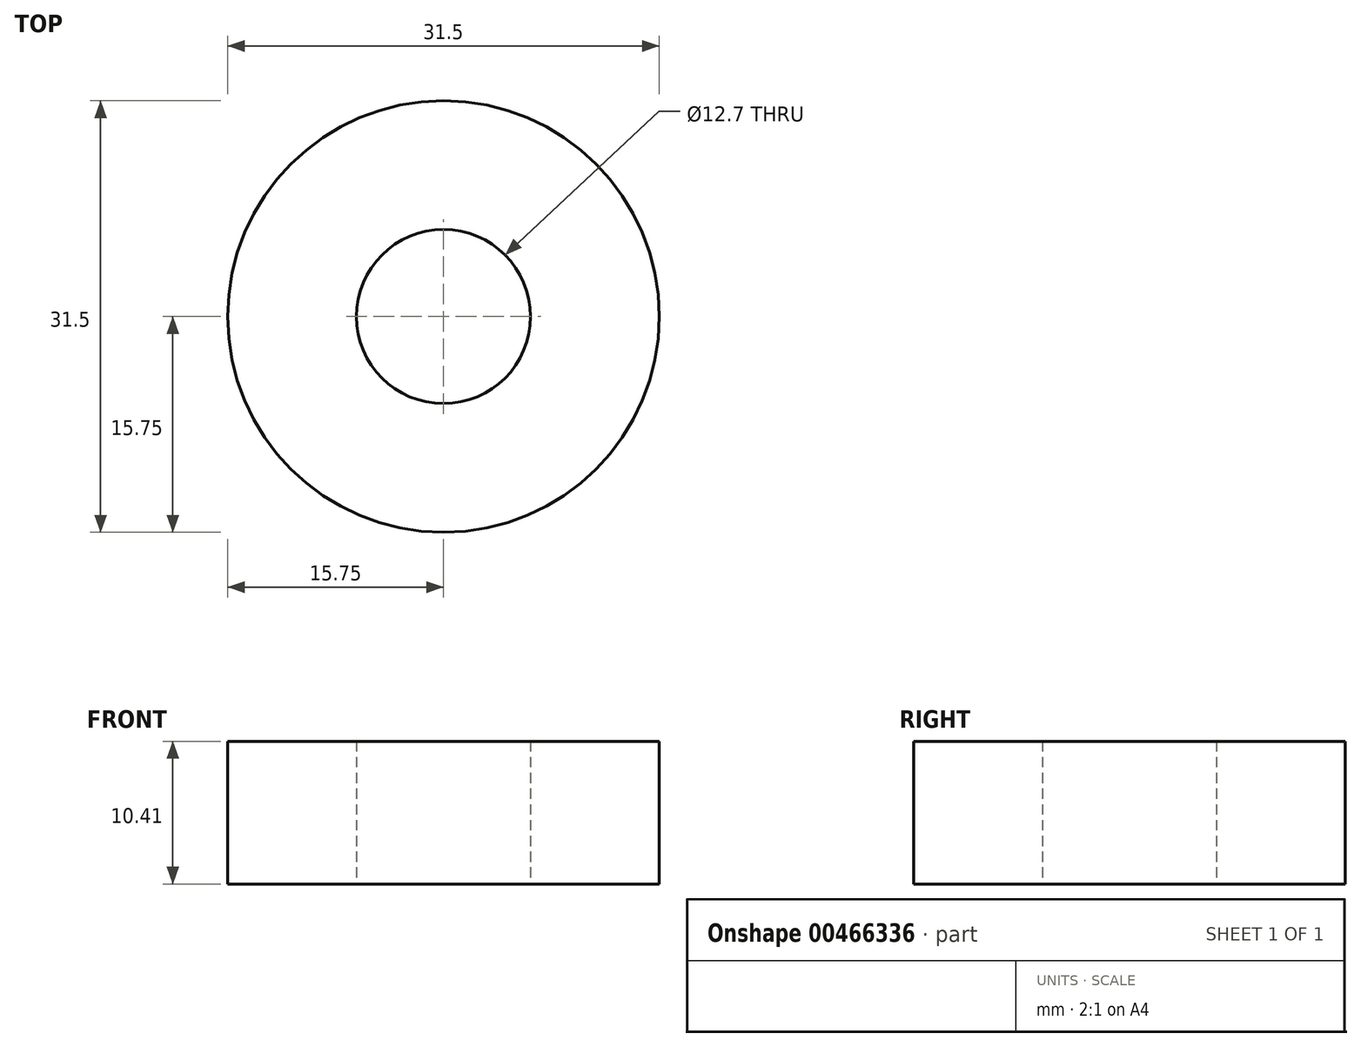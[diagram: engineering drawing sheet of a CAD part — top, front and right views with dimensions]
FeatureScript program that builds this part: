
annotation { "Feature Type Name" : "Feature", "Feature Type Description" : "" }
export const myFeature = defineFeature(function(context is Context, id is Id, definition is map)
    precondition{}
    {
        {
            var Q0;
            Q0=qCreatedBy(makeId("Top.planeOp"),FACE);
            var sketch = newSketch(context, id + "F0", { "sketchPlane" : qUnion([Q0])});
            skCircle(sketch, "E0", {"center": v(0, 0) * mm, "radius": 15.75 * mm});
            skCircle(sketch, "E1", {"center": v(0, 0) * mm, "radius": 6.35 * mm});
            skSolve(sketch);
        }
        {
            var Q0;
            Q0=makeQuery(id+"F0.imprint","IMPRINT",FACE,{"disambiguationData":[TD([[makeQuery(id+"F0.imprint","IMPRINT",EDGE,{"derivedFrom":sQuery(id+"F0.wireOp",EDGE,"E0")}),1.0]])]});
            extrude(context, id + "F1", {"entities" : qUnion([Q0]), "depth" : 10.4 * mm});
        }
    });
